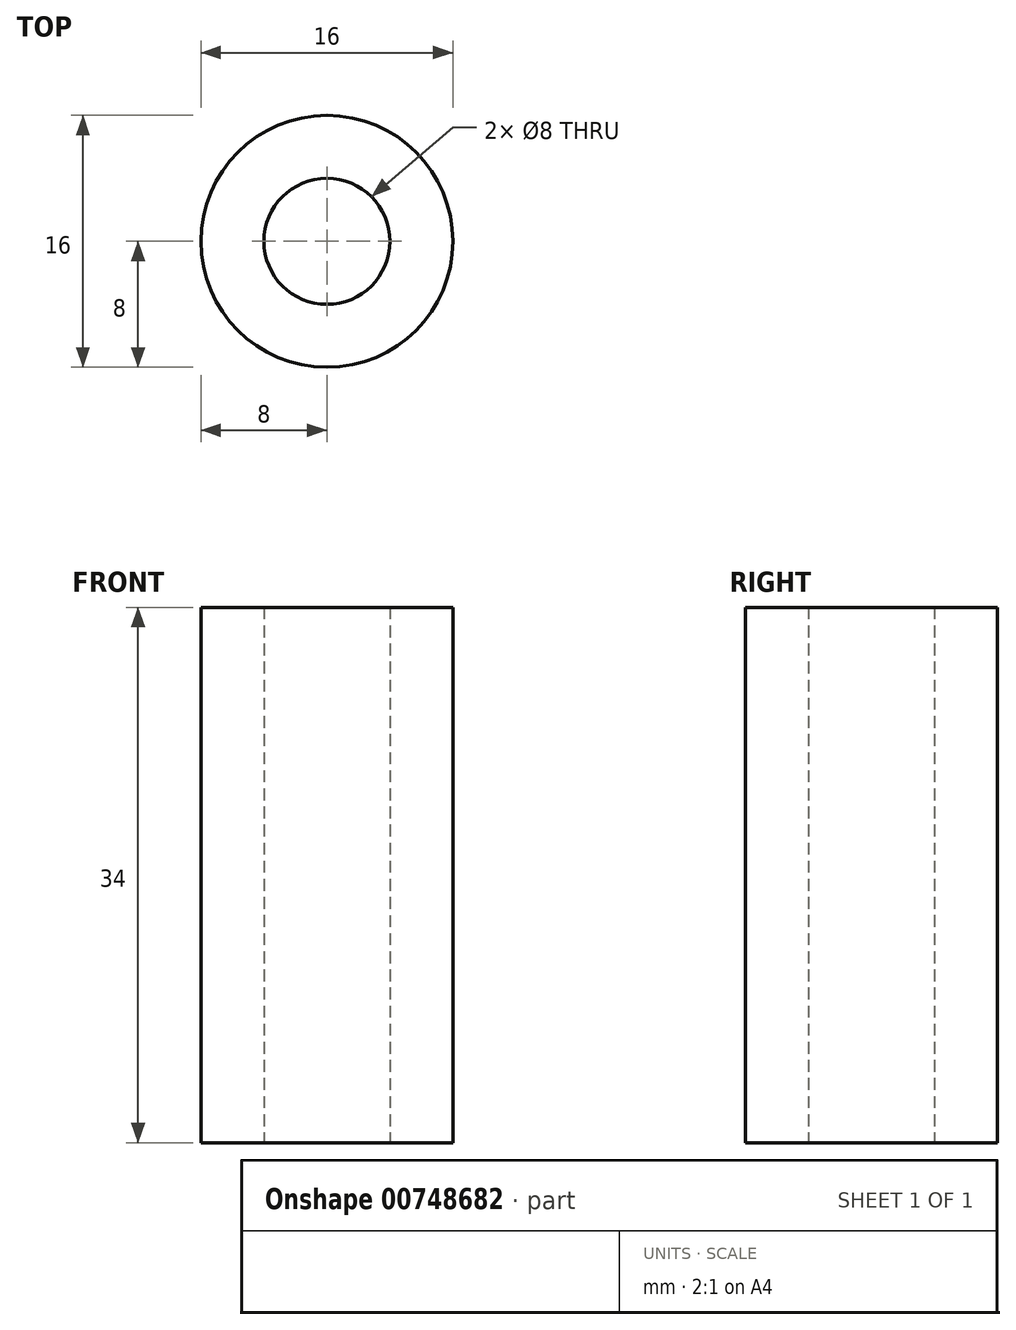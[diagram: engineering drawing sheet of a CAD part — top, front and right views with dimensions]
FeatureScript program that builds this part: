
annotation { "Feature Type Name" : "Feature", "Feature Type Description" : "" }
export const myFeature = defineFeature(function(context is Context, id is Id, definition is map)
    precondition{}
    {
        {
            var Q0;
            Q0=qCreatedBy(makeId("Top.planeOp"),FACE);
            var sketch = newSketch(context, id + "F0", { "sketchPlane" : qUnion([Q0])});
            skCircle(sketch, "E0", {"center": v(0, 0) * mm, "radius": 8 * mm});
            skCircle(sketch, "E1", {"center": v(0, 0) * mm, "radius": 4 * mm});
            skSolve(sketch);
        }
        {
            var Q0;
            Q0=makeQuery(id+"F0.imprint","IMPRINT",FACE,{"disambiguationData":[TD([[makeQuery(id+"F0.imprint","IMPRINT",EDGE,{"derivedFrom":sQuery(id+"F0.wireOp",EDGE,"E0")}),1.0]])]});
            extrude(context, id + "F1", {"entities" : qUnion([Q0]), "depth" : 34 * mm, "offsetDistance" : 25 * mm});
        }
    });
